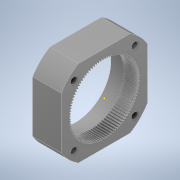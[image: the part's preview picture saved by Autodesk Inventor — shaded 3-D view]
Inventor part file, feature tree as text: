
AUTODESK INVENTOR PART (.ipt)
format: ipt  version: 2022 (Build 260153000, 153)  size: 644,608 bytes
history: mixed  units: in
note: dims shown in document units (in); Inventor stores cm internally (conversion verified against a paired STEP export)
features: sketch x4, extrude x3, other x1, imported_body x1
ambient origin geometry x8: Origin, YZ Plane, XZ Plane, XY Plane, X Axis, Y Axis, Z Axis, Center Point
bodies: Solid1 (imported_parasolid)
feature tree (9):
  extrude  "Extrusion1"  Depth=0.3937in TaperAngle=0.0deg
  extrude  "Extrusion2"  [1 undecoded]
  extrude  "Extrusion3"  [1 undecoded]
  sketch  "Sketch5"
  sketch  "Sketch2"  dims[d1=0.2756in d2=0.0in d3=0.3937in d4=0.0in]
  sketch  "Sketch3"  dims[d5=0.3937in d6=0.0in]
  sketch  "Sketch4"
  other  "96_Teeth_Gear.STEP"
  imported_body  NMx_Import_Brep_tag  [imported B-rep: ~399 faces, bbox_mm=[20.0, 60.0, 60.0]]
note: 2 required parameter values undecoded (feature->parameter linkage not recoverable at this tier; creation-order binding heuristic only, values carry confidence <= 0.55)
